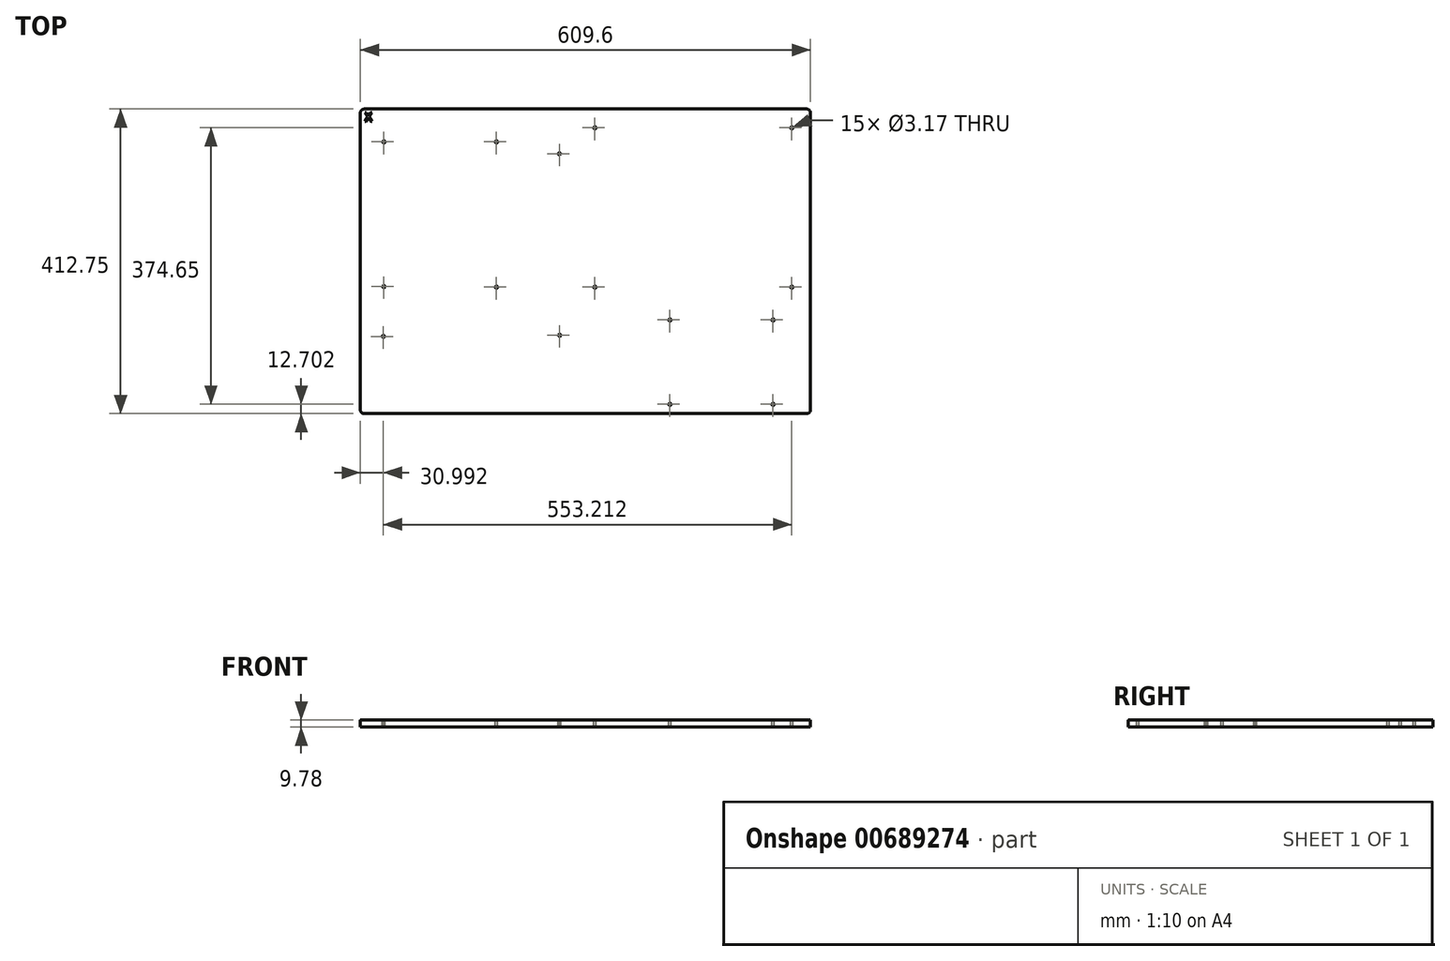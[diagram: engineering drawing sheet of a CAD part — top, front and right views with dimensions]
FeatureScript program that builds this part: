
annotation { "Feature Type Name" : "Feature", "Feature Type Description" : "" }
export const myFeature = defineFeature(function(context is Context, id is Id, definition is map)
    precondition{}
    {
        {
            var Q0;
            Q0=qCreatedBy(makeId("Top.planeOp"),FACE);
            var sketch = newSketch(context, id + "F0", { "sketchPlane" : qUnion([Q0])});
            skLineSegment(sketch, "E0.bottom", {"start": v(-301.58, 280.8) * mm, "end": v(308.02, 280.8) * mm});
            skLineSegment(sketch, "E0.top", {"start": v(-301.58, -131.96) * mm, "end": v(308.02, -131.96) * mm});
            skLineSegment(sketch, "E0.left", {"start": v(-301.58, 280.8) * mm, "end": v(-301.58, -131.96) * mm});
            skLineSegment(sketch, "E0.right", {"start": v(308.02, 280.8) * mm, "end": v(308.02, -131.96) * mm});
            skSolve(sketch);
        }
        {
            var Q0;
            Q0 = qSketchRegion(id + "F0", true);
            extrude(context, id + "F1", {"entities" : qUnion([Q0]), "depth" : 9.52 * mm, "offsetDistance" : 25.4 * mm});
        }
        {
            var Q0;
            Q0=makeQuery(id+"F1.opExtrude","CAP_FACE",FACE,{"disambiguationData":[OSD([sQuery(id+"F0.wireOp",EDGE,"E0.bottom"),sQuery(id+"F0.wireOp",EDGE,"E0.top"),sQuery(id+"F0.wireOp",EDGE,"E0.left"),sQuery(id+"F0.wireOp",EDGE,"E0.right")])],"isStart":false});
            var sketch = newSketch(context, id + "F2", { "sketchPlane" : qUnion([Q0])});
            skCircle(sketch, "E1", {"center": v(-269.83, 236.34) * mm, "radius": 1.59 * mm});
            skCircle(sketch, "E2", {"center": v(-269.83, 40.25) * mm, "radius": 1.59 * mm});
            skCircle(sketch, "E3", {"center": v(-270.59, -27.23) * mm, "radius": 1.59 * mm});
            skCircle(sketch, "E4", {"center": v(-117.43, 236.34) * mm, "radius": 1.59 * mm});
            skCircle(sketch, "E5", {"center": v(-117.43, 39.5) * mm, "radius": 1.59 * mm});
            skCircle(sketch, "E6", {"center": v(-31.7, -25.71) * mm, "radius": 1.59 * mm});
            skCircle(sketch, "E7", {"center": v(-32.08, 220.19) * mm, "radius": 1.59 * mm});
            skSolve(sketch);
        }
        {
            var Q0;
            Q0 = qSketchRegion(id + "F2", true);
            extrude(context, id + "F3", {"entities" : qUnion([Q0]), "operationType" : NewBodyOperationType.REMOVE, "oppositeDirection" : true, "depth" : 25.4 * mm, "offsetDistance" : 25.4 * mm});
        }
        {
            var Q0;
            Q0=makeQuery(id+"F1.opExtrude","CAP_FACE",FACE,{"disambiguationData":[OSD([sQuery(id+"F0.wireOp",EDGE,"E0.bottom"),sQuery(id+"F0.wireOp",EDGE,"E0.top"),sQuery(id+"F0.wireOp",EDGE,"E0.left"),sQuery(id+"F0.wireOp",EDGE,"E0.right")])],"isStart":false});
            var sketch = newSketch(context, id + "F4", { "sketchPlane" : qUnion([Q0])});
            skLineSegment(sketch, "E8.bottom", {"start": v(117.52, -4.96) * mm, "end": v(257.22, -4.96) * mm, "construction": true});
            skLineSegment(sketch, "E8.top", {"start": v(117.52, -119.26) * mm, "end": v(257.22, -119.26) * mm, "construction": true});
            skLineSegment(sketch, "E8.left", {"start": v(117.52, -4.96) * mm, "end": v(117.52, -119.26) * mm, "construction": true});
            skLineSegment(sketch, "E8.right", {"start": v(257.22, -4.96) * mm, "end": v(257.22, -119.26) * mm, "construction": true});
            skPoint(sketch, "E9", {"position": v(117.52, -4.96) * mm});
            skPoint(sketch, "E10", {"position": v(257.22, -4.96) * mm});
            skPoint(sketch, "E11", {"position": v(257.22, -119.26) * mm});
            skPoint(sketch, "E12", {"position": v(117.52, -119.26) * mm});
            skSolve(sketch);
        }
        {
            var Q0;
            Q0=sQuery(id+"F4.wireOp",VERTEX,"E9");
            var Q1;
            Q1=sQuery(id+"F4.wireOp",VERTEX,"E10");
            var Q2;
            Q2=sQuery(id+"F4.wireOp",VERTEX,"E11");
            var Q3;
            Q3=sQuery(id+"F4.wireOp",VERTEX,"E12");
            var Q4;
            Q4=makeQuery(id+"F1.opExtrude","SWEPT_BODY",BODY,{"disambiguationData":[OSD([sQuery(id+"F0.wireOp",EDGE,"E0.bottom"),sQuery(id+"F0.wireOp",EDGE,"E0.top"),sQuery(id+"F0.wireOp",EDGE,"E0.left"),sQuery(id+"F0.wireOp",EDGE,"E0.right")])]});
            hole(context, id + "F5", {"style" : HoleStyle.SIMPLE, "endStyle" : HoleEndStyle.THROUGH, "holeDiameter" : 3.17 * mm, "majorDiameter" : 6.35 * mm, "isTappedThrough" : true, "tappedDepth" : 12.7 * mm, "tapClearance" : 3, "locations" : qUnion([Q0, Q1, Q2, Q3]), "scope" : qUnion([Q4])});
        }
        {
            var Q0;
            Q0=makeQuery(id+"F1.opExtrude","CAP_FACE",FACE,{"disambiguationData":[OSD([sQuery(id+"F0.wireOp",EDGE,"E0.bottom"),sQuery(id+"F0.wireOp",EDGE,"E0.top"),sQuery(id+"F0.wireOp",EDGE,"E0.left"),sQuery(id+"F0.wireOp",EDGE,"E0.right")])],"isStart":false});
            var sketch = newSketch(context, id + "F6", { "sketchPlane" : qUnion([Q0])});
            skLineSegment(sketch, "E13.bottom", {"start": v(15.92, 255.4) * mm, "end": v(282.62, 255.4) * mm, "construction": true});
            skLineSegment(sketch, "E13.top", {"start": v(15.92, 39.5) * mm, "end": v(282.62, 39.5) * mm, "construction": true});
            skLineSegment(sketch, "E13.left", {"start": v(15.92, 255.4) * mm, "end": v(15.92, 39.5) * mm, "construction": true});
            skLineSegment(sketch, "E13.right", {"start": v(282.62, 255.4) * mm, "end": v(282.62, 39.5) * mm, "construction": true});
            skPoint(sketch, "E14", {"position": v(15.92, 255.4) * mm});
            skPoint(sketch, "E15", {"position": v(282.62, 255.4) * mm});
            skPoint(sketch, "E16", {"position": v(282.62, 39.5) * mm});
            skPoint(sketch, "E17", {"position": v(15.92, 39.5) * mm});
            skSolve(sketch);
        }
        {
            var Q0;
            Q0=sQuery(id+"F6.wireOp",VERTEX,"E14");
            var Q1;
            Q1=sQuery(id+"F6.wireOp",VERTEX,"E15");
            var Q2;
            Q2=sQuery(id+"F6.wireOp",VERTEX,"E16");
            var Q3;
            Q3=sQuery(id+"F6.wireOp",VERTEX,"E17");
            var Q4;
            Q4=makeQuery(id+"F1.opExtrude","SWEPT_BODY",BODY,{"disambiguationData":[OSD([sQuery(id+"F0.wireOp",EDGE,"E0.bottom"),sQuery(id+"F0.wireOp",EDGE,"E0.top"),sQuery(id+"F0.wireOp",EDGE,"E0.left"),sQuery(id+"F0.wireOp",EDGE,"E0.right")])]});
            hole(context, id + "F7", {"style" : HoleStyle.SIMPLE, "endStyle" : HoleEndStyle.THROUGH, "holeDiameter" : 3.17 * mm, "majorDiameter" : 6.35 * mm, "isTappedThrough" : true, "tappedDepth" : 12.7 * mm, "tapClearance" : 3, "locations" : qUnion([Q0, Q1, Q2, Q3]), "scope" : qUnion([Q4])});
        }
        {
            var Q0;
            Q0=makeQuery(id+"F1.opExtrude","SWEPT_EDGE",EDGE,{"disambiguationData":[OSD([sQuery(id+"F0.wireOp",EDGE,"E0.top"),sQuery(id+"F0.wireOp",EDGE,"E0.left")])]});
            var Q1;
            Q1=makeQuery(id+"F1.opExtrude","SWEPT_EDGE",EDGE,{"disambiguationData":[OSD([sQuery(id+"F0.wireOp",EDGE,"E0.bottom"),sQuery(id+"F0.wireOp",EDGE,"E0.left")])]});
            var Q2;
            Q2=makeQuery(id+"F1.opExtrude","SWEPT_EDGE",EDGE,{"disambiguationData":[OSD([sQuery(id+"F0.wireOp",EDGE,"E0.bottom"),sQuery(id+"F0.wireOp",EDGE,"E0.right")])]});
            var Q3;
            Q3=makeQuery(id+"F1.opExtrude","SWEPT_EDGE",EDGE,{"disambiguationData":[OSD([sQuery(id+"F0.wireOp",EDGE,"E0.top"),sQuery(id+"F0.wireOp",EDGE,"E0.right")])]});
            fillet(context, id + "F8", {"entities" : qUnion([Q0, Q1, Q2, Q3]), "radius" : 5.08 * mm, "tangentPropagation" : true, "allowEdgeOverflow" : false});
        }
        {
            var Q0;
            Q0=makeQuery(id+"F1.opExtrude","CAP_FACE",FACE,{"disambiguationData":[OSD([sQuery(id+"F0.wireOp",EDGE,"E0.bottom"),sQuery(id+"F0.wireOp",EDGE,"E0.top"),sQuery(id+"F0.wireOp",EDGE,"E0.left"),sQuery(id+"F0.wireOp",EDGE,"E0.right")])],"isStart":false});
            var sketch = newSketch(context, id + "F9", { "sketchPlane" : qUnion([Q0])});
            skText(sketch, "E18", { "text": "X", "fontName": "OpenSans-Regular.ttf"});
            const initialGuessF9  = {"E18": [-0.29569, 0.26383, 1, 0, 0.0125]};
            skSetInitialGuess(sketch, initialGuessF9);
            skSolve(sketch);
        }
        {
            var Q0;
            Q0 = qSketchRegion(id + "F9", true);
            extrude(context, id + "F10", {"entities" : qUnion([Q0]), "operationType" : NewBodyOperationType.ADD, "depth" : 0.25 * mm, "offsetDistance" : 25.4 * mm});
        }
    });
